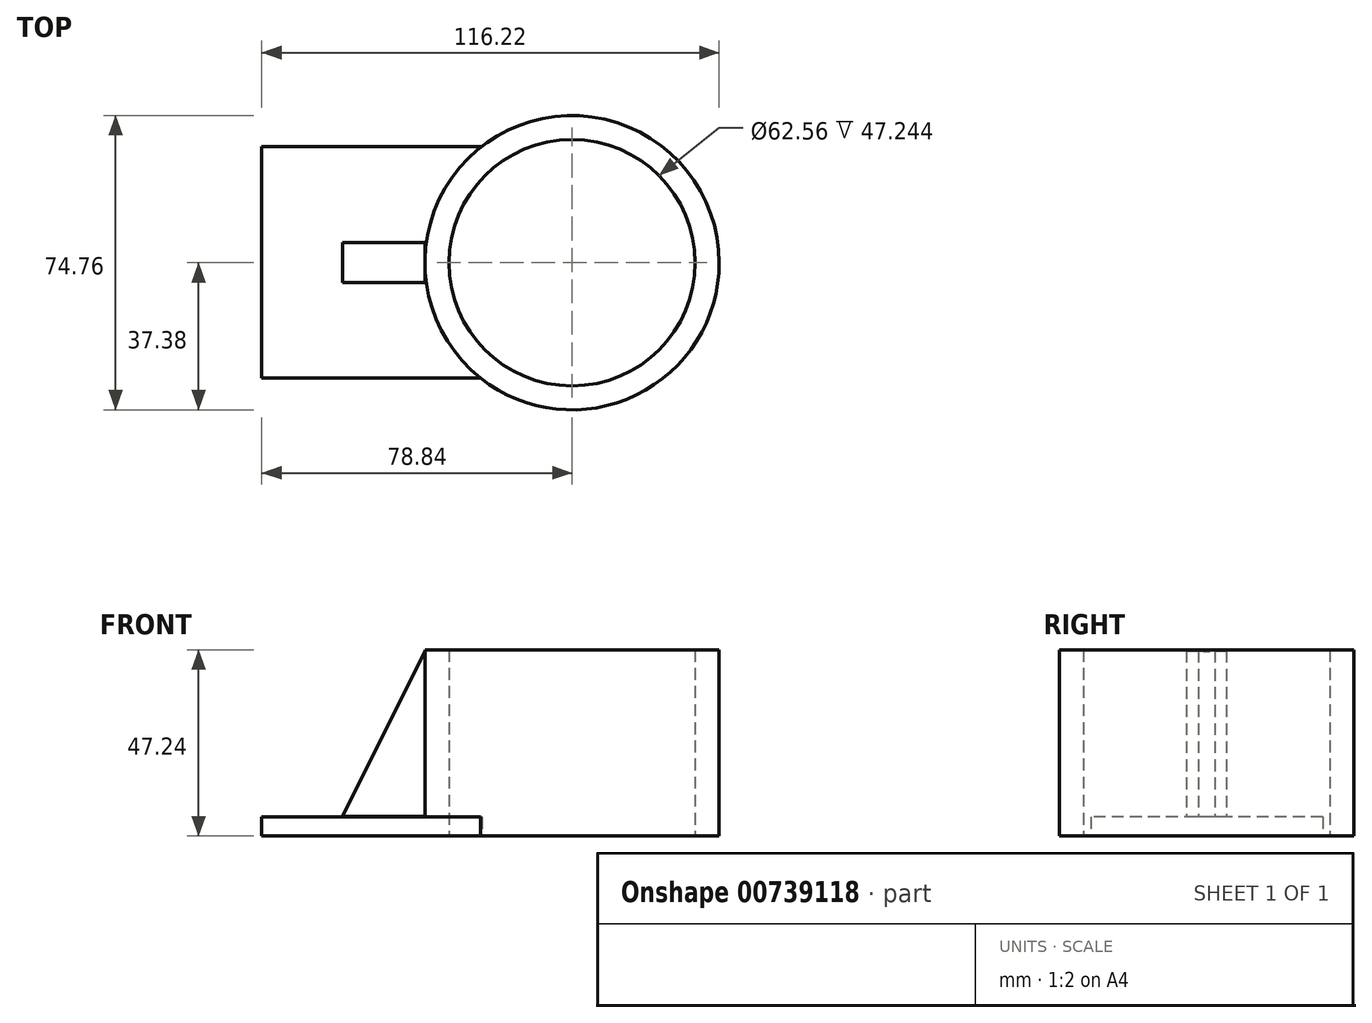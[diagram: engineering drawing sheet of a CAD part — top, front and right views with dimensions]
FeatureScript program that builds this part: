
annotation { "Feature Type Name" : "Feature", "Feature Type Description" : "" }
export const myFeature = defineFeature(function(context is Context, id is Id, definition is map)
    precondition{}
    {
        {
            var Q0;
            Q0=qCreatedBy(makeId("Top.planeOp"),FACE);
            var sketch = newSketch(context, id + "F0", { "sketchPlane" : qUnion([Q0])});
            skCircle(sketch, "E0", {"center": v(0, 0) * mm, "radius": 37.38 * mm});
            skCircle(sketch, "E1", {"center": v(0, 0) * mm, "radius": 31.28 * mm});
            skLineSegment(sketch, "E2.bottom", {"start": v(-22.92, 29.53) * mm, "end": v(-78.84, 29.53) * mm});
            skLineSegment(sketch, "E2.top", {"start": v(-22.92, -29.32) * mm, "end": v(-78.84, -29.32) * mm});
            skLineSegment(sketch, "E2.left", {"start": v(-22.92, 29.53) * mm, "end": v(-22.92, -29.32) * mm});
            skLineSegment(sketch, "E2.right", {"start": v(-78.84, 29.53) * mm, "end": v(-78.84, -29.32) * mm});
            skSolve(sketch);
        }
        {
            var Q0;
            {var subQ0=sQuery(id+"F0.wireOp",EDGE,"E2.left");var subQ3=sQuery(id+"F0.wireOp",EDGE,"E1");var subQ4=makeQuery(id+"F0.imprint","INTERSECT",VERTEX,{"disambiguationData":[OD(0.0)],"derivedFrom":[subQ3,subQ0]});Q0=makeQuery(id+"F0.imprint","IMPRINT",FACE,{"disambiguationData":[TD([[makeQuery(id+"F0.imprint","IMPRINT",EDGE,{"disambiguationData":[TD([[subQ4,1.0]])],"derivedFrom":subQ3}),-1.0]])]});}
            var Q1;
            {var subQ0=sQuery(id+"F0.wireOp",EDGE,"E2.left");var subQ3=sQuery(id+"F0.wireOp",EDGE,"E1");var subQ4=makeQuery(id+"F0.imprint","INTERSECT",VERTEX,{"disambiguationData":[OD(0.0)],"derivedFrom":[subQ3,subQ0]});Q1=makeQuery(id+"F0.imprint","IMPRINT",FACE,{"disambiguationData":[TD([[makeQuery(id+"F0.imprint","IMPRINT",EDGE,{"disambiguationData":[TD([[subQ4,-1.0]])],"derivedFrom":subQ3}),-1.0]])]});}
            extrude(context, id + "F1", {"entities" : qUnion([Q0, Q1]), "depth" : 47.24 * mm, "offsetDistance" : 25.4 * mm});
        }
        {
            var Q0;
            {var subQ0=sQuery(id+"F0.wireOp",EDGE,"E2.bottom");Q0=makeQuery(id+"F0.imprint","IMPRINT",FACE,{"disambiguationData":[TD([[makeQuery(id+"F0.imprint","IMPRINT",EDGE,{"derivedFrom":subQ0}),1.0]])]});}
            extrude(context, id + "F2", {"entities" : qUnion([Q0]), "operationType" : NewBodyOperationType.ADD, "depth" : 4.83 * mm, "offsetDistance" : 25.4 * mm});
        }
        {
            var Q0;
            Q0=qCreatedBy(makeId("Front.planeOp"),FACE);
            var sketch = newSketch(context, id + "F3", { "sketchPlane" : qUnion([Q0])});
            skLineSegment(sketch, "E3", {"start": v(-37.32, 47.03) * mm, "end": v(-37.32, 4.99) * mm});
            skLineSegment(sketch, "E4", {"start": v(-37.32, 4.99) * mm, "end": v(-58.3, 4.99) * mm});
            skLineSegment(sketch, "E5", {"start": v(-37.32, 47.03) * mm, "end": v(-58.3, 4.99) * mm});
            skSolve(sketch);
        }
        {
            var Q0;
            Q0 = qSketchRegion(id + "F3", true);
            extrude(context, id + "F4", {"entities" : qUnion([Q0]), "operationType" : NewBodyOperationType.ADD, "endBound" : BoundingType.SYMMETRIC, "depth" : 10.16 * mm, "offsetDistance" : 25.4 * mm});
        }
    });
